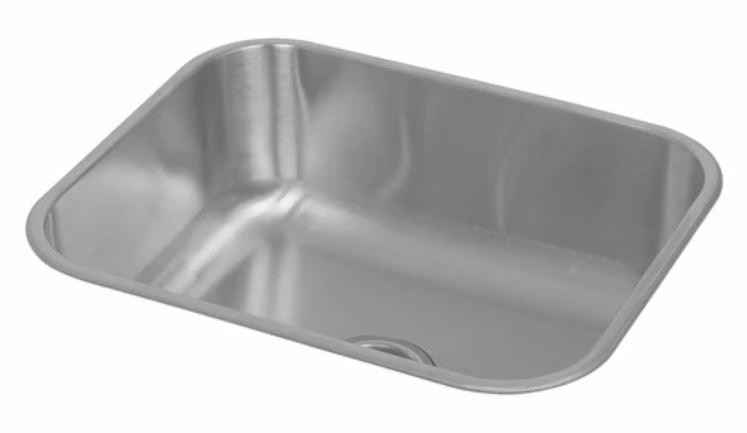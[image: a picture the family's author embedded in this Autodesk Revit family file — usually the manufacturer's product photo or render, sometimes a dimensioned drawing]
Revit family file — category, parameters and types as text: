
# Revit family: 01-31703-11 LAVAPLATOS EN ACERO POCETA 53 X 43 CM
name_source: partatom
category: Aparatos sanitarios
revit_build: Autodesk Revit 2018 (Build: 20170223_1515(x64)
units: mm (PartAtom-declared; Revit-internal decimal feet)

## family parameters
Anfitrión = Cara
Compartido = No
Corte con vacíos al cargar = No
Cota de conector redondo = Diámetro de uso
Número OmniClass = 23.31.11.00
Punto de cálculo de habitación = No
Tipo de pieza = Normal

## types (1)
- 01-31703-11
    Acero inox = Acero inoxidable
    Alto = 170 mm
    Ancho = 530 mm
    Conexión AC = Sí
    Conexión AF = Sí
    Conexión de residuos = No
    Conexión de ventilación = No
    Descripción = Lavaplatos en acero
    Elevación por defecto = 0 mm  [stored 0 ft]
    Fabricante = Gricol
    Imagen de tipo = LAVAPLATOS EN ACERO POCETA 53 X 43 CM.JPG
    Largo = 430 mm
    Link Ficha Tecnica = No existe
    Modelo = 01-31703-11
    Product Name = LAVAPLATOS EN ACERO POCETA 53 X 43 CM
    URL = https://www.gricol.com

note: [stored X ft] marks values corroborated as IEEE doubles in the binary element streams (Revit-internal decimal feet)

## geometry (parser evidence)
native form markers: Blend x2, Sweep x12
no freeform markers — native parametric forms only
